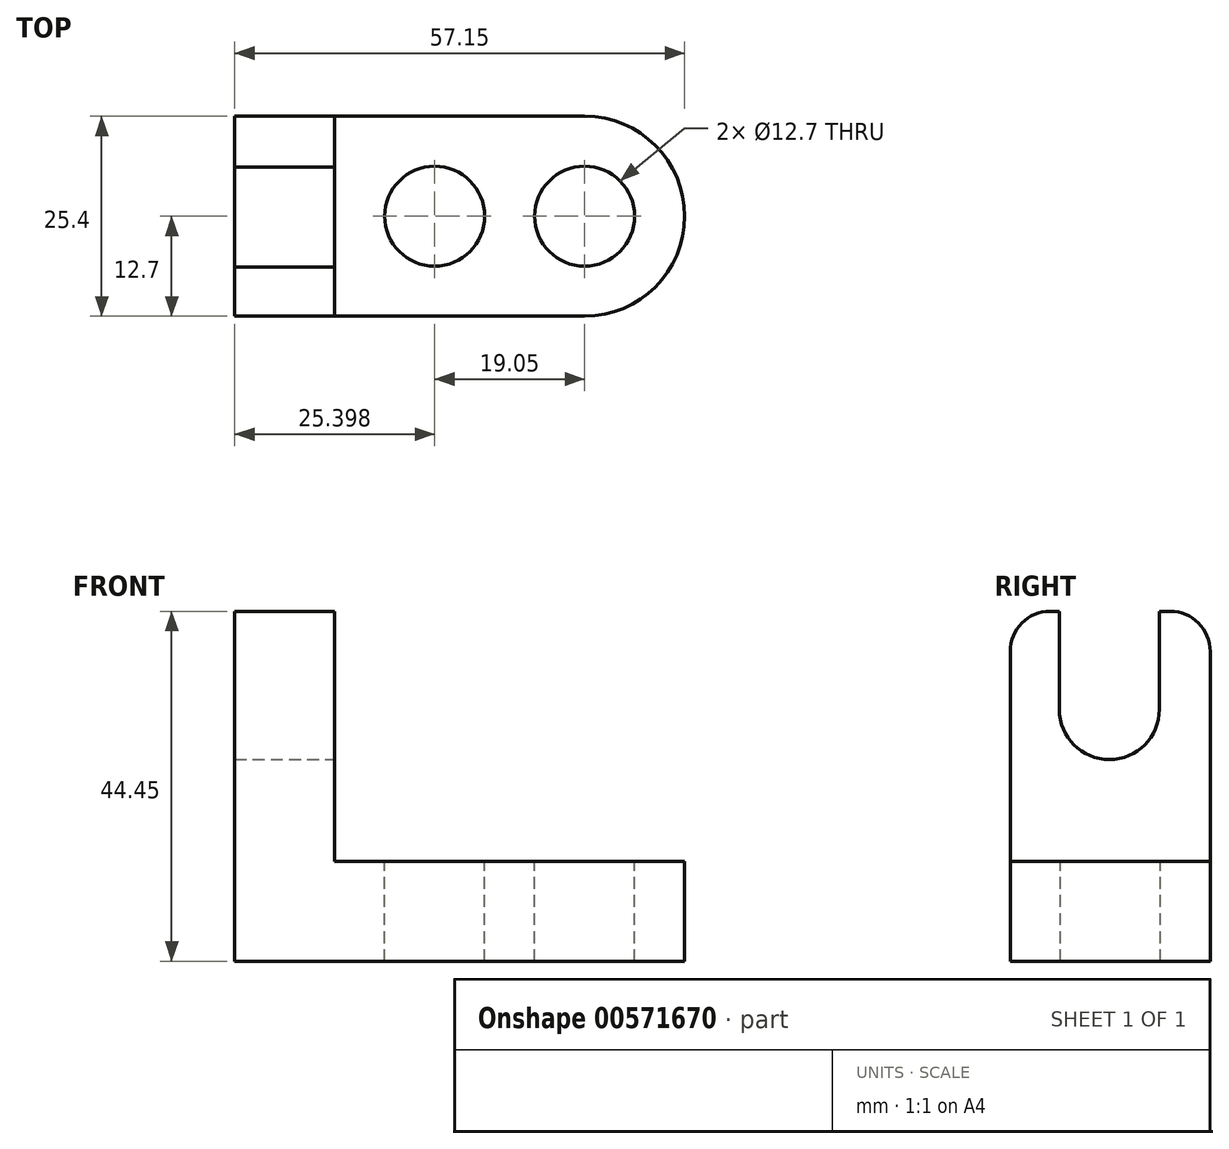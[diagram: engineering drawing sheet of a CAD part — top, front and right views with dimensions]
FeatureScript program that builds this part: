
annotation { "Feature Type Name" : "Feature", "Feature Type Description" : "" }
export const myFeature = defineFeature(function(context is Context, id is Id, definition is map)
    precondition{}
    {
        {
            var Q0;
            Q0=qCreatedBy(makeId("Front.planeOp"),FACE);
            var sketch = newSketch(context, id + "F0", { "sketchPlane" : qUnion([Q0])});
            skLineSegment(sketch, "E0", {"start": v(-34.9, 30.52) * mm, "end": v(-34.9, -13.93) * mm});
            skLineSegment(sketch, "E1", {"start": v(-34.9, -13.93) * mm, "end": v(9.56, -13.93) * mm});
            skLineSegment(sketch, "E2", {"start": v(9.56, -13.93) * mm, "end": v(9.56, -1.23) * mm});
            skLineSegment(sketch, "E3", {"start": v(9.56, -1.23) * mm, "end": v(-22.2, -1.23) * mm});
            skLineSegment(sketch, "E4", {"start": v(-22.2, -1.23) * mm, "end": v(-22.2, 30.52) * mm});
            skLineSegment(sketch, "E5", {"start": v(-22.2, 30.52) * mm, "end": v(-34.9, 30.52) * mm});
            skSolve(sketch);
        }
        {
            var Q0;
            Q0=makeQuery(id+"F0.imprint","IMPRINT",FACE,{"disambiguationData":[TD([[makeQuery(id+"F0.imprint","IMPRINT",EDGE,{"derivedFrom":sQuery(id+"F0.wireOp",EDGE,"E0")}),1.0]])]});
            extrude(context, id + "F1", {"entities" : qUnion([Q0]), "depth" : 25.4 * mm, "offsetDistance" : 25.4 * mm});
        }
        {
            var Q0;
            Q0=makeQuery(id+"F1.opExtrude","SWEPT_FACE",FACE,{"disambiguationData":[OSD([sQuery(id+"F0.wireOp",EDGE,"E3")])]});
            var sketch = newSketch(context, id + "F2", { "sketchPlane" : qUnion([Q0])});
            skArc(sketch, "E6", {"start": v(9.56, -25.4) * mm, "mid": v(22.26, -12.7) * mm, "end": v(9.56, 0) * mm});
            skSolve(sketch);
        }
        {
            var Q0;
            Q0=makeQuery(id+"F2.imprint","IMPRINT",FACE,{"disambiguationData":[TD([[makeQuery(id+"F2.imprint","IMPRINT",EDGE,{"derivedFrom":sQuery(id+"F2.wireOp",EDGE,"E6")}),1.0]])]});
            extrude(context, id + "F3", {"entities" : qUnion([Q0]), "operationType" : NewBodyOperationType.ADD, "oppositeDirection" : true, "depth" : 12.7 * mm, "offsetDistance" : 25.4 * mm});
        }
        {
            var Q0;
            {var subQ0=sQuery(id+"F0.wireOp",EDGE,"E3");Q0=makeQuery(id+"F3.boolean.opBoolean","MERGE",FACE,{"derivedFrom":[makeQuery(id+"F1.opExtrude","SWEPT_FACE",FACE,{"disambiguationData":[OSD([subQ0])]}),makeQuery(id+"F3.opExtrude","CAP_FACE",FACE,{"disambiguationData":[OSD([sQuery(id+"F0.wireOp",EDGE,"E2"),subQ0,sQuery(id+"F2.wireOp",EDGE,"E6")])],"isStart":true})]});}
            var sketch = newSketch(context, id + "F4", { "sketchPlane" : qUnion([Q0])});
            skCircle(sketch, "E7", {"center": v(9.56, -12.7) * mm, "radius": 6.35 * mm});
            skCircle(sketch, "E8", {"center": v(-9.5, -12.7) * mm, "radius": 6.35 * mm});
            skPoint(sketch, "E8.centerSnap0", {"position": v(-22.2, -12.7) * mm});
            skSolve(sketch);
        }
        {
            var Q0;
            Q0=makeQuery(id+"F4.imprint","IMPRINT",FACE,{"disambiguationData":[TD([[makeQuery(id+"F4.imprint","IMPRINT",EDGE,{"derivedFrom":sQuery(id+"F4.wireOp",EDGE,"E7")}),1.0]])]});
            var Q1;
            Q1=makeQuery(id+"F4.imprint","IMPRINT",FACE,{"disambiguationData":[TD([[makeQuery(id+"F4.imprint","IMPRINT",EDGE,{"derivedFrom":sQuery(id+"F4.wireOp",EDGE,"E8")}),1.0]])]});
            extrude(context, id + "F5", {"entities" : qUnion([Q0, Q1]), "operationType" : NewBodyOperationType.REMOVE, "oppositeDirection" : true, "depth" : 42.67 * mm, "offsetDistance" : 25.4 * mm});
        }
        {
            var Q0;
            Q0=makeQuery(id+"F1.opExtrude","SWEPT_FACE",FACE,{"disambiguationData":[OSD([sQuery(id+"F0.wireOp",EDGE,"E4")])]});
            var sketch = newSketch(context, id + "F6", { "sketchPlane" : qUnion([Q0])});
            skSolve(sketch);
        }
        {
            var Q0;
            Q0=makeQuery(id+"F1.opExtrude","CAP_EDGE",EDGE,{"disambiguationData":[OSD([sQuery(id+"F0.wireOp",EDGE,"E5")])],"isStart":false});
            var Q1;
            Q1=makeQuery(id+"F1.opExtrude","CAP_EDGE",EDGE,{"disambiguationData":[OSD([sQuery(id+"F0.wireOp",EDGE,"E5")])],"isStart":true});
            fillet(context, id + "F7", {"entities" : qUnion([Q0, Q1]), "radius" : 5.08 * mm, "tangentPropagation" : true, "allowEdgeOverflow" : false});
        }
        {
            var Q0;
            {var subQ0=sQuery(id+"F0.wireOp",EDGE,"E4");Q0=makeQuery(id+"F6.imprint","IMPRINT",FACE,{"disambiguationData":[TD([[makeQuery(id+"F6.imprint","IMPRINT",EDGE,{"derivedFrom":makeQuery(id+"F1.opExtrude","CAP_EDGE",EDGE,{"disambiguationData":[OSD([subQ0])],"isStart":true})}),1.0]])]});}
            var sketch = newSketch(context, id + "F8", { "sketchPlane" : qUnion([Q0])});
            skLineSegment(sketch, "E9", {"start": v(-6.45, 30.75) * mm, "end": v(-6.45, 18.05) * mm});
            skLineSegment(sketch, "E10", {"start": v(-19.15, 30.75) * mm, "end": v(-19.15, 18.05) * mm});
            skArc(sketch, "E11", {"start": v(-19.15, 18.05) * mm, "mid": v(-12.8, 11.7) * mm, "end": v(-6.45, 18.05) * mm});
            skSolve(sketch);
        }
        {
            var Q0;
            {var subQ0=sQuery(id+"F8.wireOp",EDGE,"E11");Q0=makeQuery(id+"F8.imprint","IMPRINT",FACE,{"disambiguationData":[TD([[makeQuery(id+"F8.imprint","IMPRINT",EDGE,{"derivedFrom":subQ0}),1.0]])]});}
            extrude(context, id + "F9", {"entities" : qUnion([Q0]), "operationType" : NewBodyOperationType.REMOVE, "oppositeDirection" : true, "depth" : 25.4 * mm, "offsetDistance" : 25.4 * mm});
        }
    });
